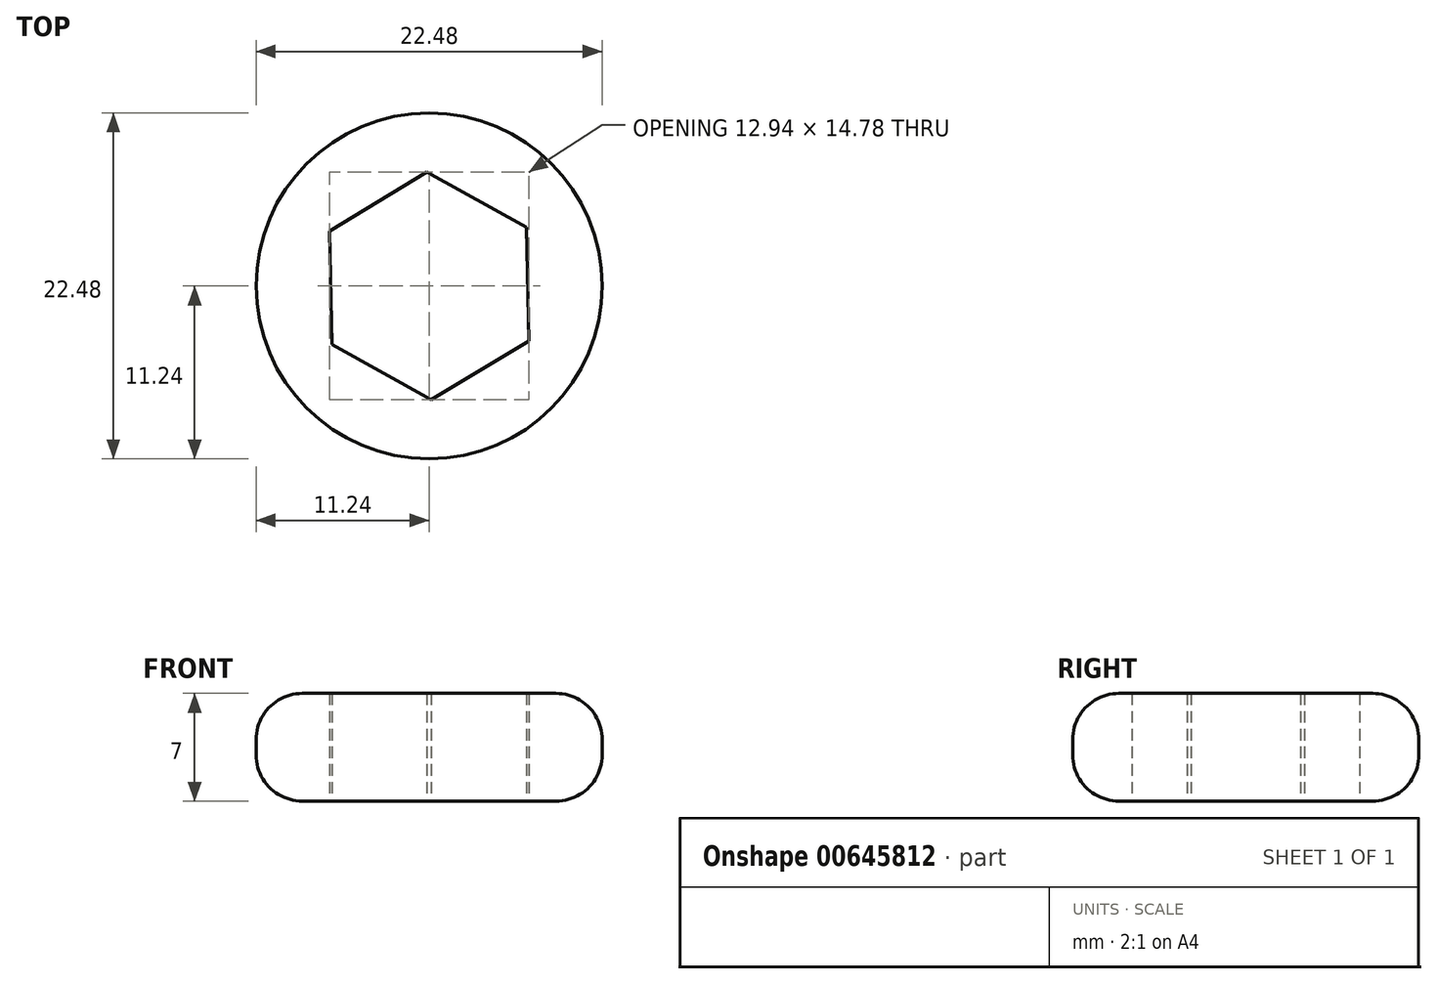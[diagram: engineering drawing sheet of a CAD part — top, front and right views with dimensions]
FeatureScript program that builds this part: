
annotation { "Feature Type Name" : "Feature", "Feature Type Description" : "" }
export const myFeature = defineFeature(function(context is Context, id is Id, definition is map)
    precondition{}
    {
        {
            var Q0;
            Q0=qCreatedBy(makeId("Top.planeOp"),FACE);
            var sketch = newSketch(context, id + "F0", { "sketchPlane" : qUnion([Q0])});
            skCircle(sketch, "E0.cCircle", {"center": v(25, 0) * mm, "radius": 6.4 * mm, "construction": true});
            skLineSegment(sketch, "E0.0", {"start": v(31.47, -3.57) * mm, "end": v(25.14, -7.39) * mm});
            skLineSegment(sketch, "E0.1", {"start": v(25.14, -7.39) * mm, "end": v(18.67, -3.82) * mm});
            skLineSegment(sketch, "E0.2", {"start": v(18.67, -3.82) * mm, "end": v(18.53, 3.57) * mm});
            skLineSegment(sketch, "E0.3", {"start": v(18.53, 3.57) * mm, "end": v(24.86, 7.39) * mm});
            skLineSegment(sketch, "E0.4", {"start": v(24.86, 7.39) * mm, "end": v(31.33, 3.82) * mm});
            skLineSegment(sketch, "E0.5", {"start": v(31.33, 3.82) * mm, "end": v(31.47, -3.57) * mm});
            skPoint(sketch, "E0.0.midPoint", {"position": v(28.3, -5.48) * mm});
            skCircle(sketch, "E1", {"center": v(25, 0) * mm, "radius": 11.24 * mm});
            skArc(sketch, "E2", {"start": v(19.83, -9.98) * mm, "mid": v(16.98, -9.1) * mm, "end": v(14.27, -10.34) * mm});
            skArc(sketch, "E3.MirrorCS", {"start": v(19.83, 9.98) * mm, "mid": v(16.98, 9.1) * mm, "end": v(14.27, 10.34) * mm});
            skCircle(sketch, "E4", {"center": v(0, 0) * mm, "radius": 0.5 * mm});
            skSolve(sketch);
        }
        {
            var Q0;
            {var subQ0=sQuery(id+"F0.wireOp",EDGE,"8972d055-53f9-408d-872e-5fed29d23d3c.2.6");var subQ1=sQuery(id+"F0.wireOp",EDGE,"8972d055-53f9-408d-872e-5fed29d23d3c.1.7");var subQ2=makeQuery(id+"F0.imprint","INTERSECT",VERTEX,{"derivedFrom":[subQ1,subQ0]});Q0=makeQuery(id+"F0.imprint","IMPRINT",FACE,{"disambiguationData":[TD([[makeQuery(id+"F0.imprint","IMPRINT",EDGE,{"disambiguationData":[TD([[subQ2,1.0]])],"derivedFrom":subQ1}),-1.0]])]});}
            var Q1;
            {var subQ0=sQuery(id+"F0.wireOp",EDGE,"8972d055-53f9-408d-872e-5fed29d23d3c.1.12");var subQ1=sQuery(id+"F0.wireOp",EDGE,"8972d055-53f9-408d-872e-5fed29d23d3c.1.10");var subQ2=makeQuery(id+"F0.imprint","INTERSECT",VERTEX,{"disambiguationData":[OD(1.0)],"derivedFrom":[subQ1,subQ0]});Q1=makeQuery(id+"F0.imprint","IMPRINT",FACE,{"disambiguationData":[TD([[makeQuery(id+"F0.imprint","IMPRINT",EDGE,{"disambiguationData":[TD([[subQ2,-1.0]])],"derivedFrom":subQ1}),-1.0]])]});}
            var Q2;
            {var subQ0=sQuery(id+"F0.wireOp",EDGE,"8972d055-53f9-408d-872e-5fed29d23d3c.2.12");var subQ1=sQuery(id+"F0.wireOp",EDGE,"8972d055-53f9-408d-872e-5fed29d23d3c.2.6");var subQ2=makeQuery(id+"F0.imprint","INTERSECT",VERTEX,{"derivedFrom":[subQ1,subQ0]});Q2=makeQuery(id+"F0.imprint","IMPRINT",FACE,{"disambiguationData":[TD([[makeQuery(id+"F0.imprint","IMPRINT",EDGE,{"disambiguationData":[TD([[subQ2,1.0]])],"derivedFrom":subQ1}),-1.0]])]});}
            var Q3;
            Q3=makeQuery(id+"F0.imprint","IMPRINT",FACE,{"disambiguationData":[TD([[makeQuery(id+"F0.imprint","IMPRINT",EDGE,{"derivedFrom":sQuery(id+"F0.wireOp",EDGE,"8972d055-53f9-408d-872e-5fed29d23d3c.1.0")}),1.0]])]});
            var Q4;
            {var subQ0=sQuery(id+"F0.wireOp",EDGE,"8972d055-53f9-408d-872e-5fed29d23d3c.2.6");var subQ1=sQuery(id+"F0.wireOp",EDGE,"8972d055-53f9-408d-872e-5fed29d23d3c.1.10");var subQ2=makeQuery(id+"F0.imprint","INTERSECT",VERTEX,{"disambiguationData":[OD(0.0)],"derivedFrom":[subQ1,subQ0]});Q4=makeQuery(id+"F0.imprint","IMPRINT",FACE,{"disambiguationData":[TD([[makeQuery(id+"F0.imprint","IMPRINT",EDGE,{"disambiguationData":[TD([[subQ2,-1.0]])],"derivedFrom":subQ1}),1.0]])]});}
            var Q5;
            Q5=makeQuery(id+"F0.imprint","IMPRINT",FACE,{"disambiguationData":[TD([[makeQuery(id+"F0.imprint","IMPRINT",EDGE,{"derivedFrom":sQuery(id+"F0.wireOp",EDGE,"8972d055-53f9-408d-872e-5fed29d23d3c.2.4")}),-1.0]])]});
            var Q6;
            Q6=makeQuery(id+"F0.imprint","IMPRINT",FACE,{"disambiguationData":[TD([[makeQuery(id+"F0.imprint","IMPRINT",EDGE,{"derivedFrom":sQuery(id+"F0.wireOp",EDGE,"E0.0")}),1.0]])]});
            var Q7;
            {var subQ0=sQuery(id+"F0.wireOp",EDGE,"E3.MirrorCS");var subQ1=sQuery(id+"F0.wireOp",EDGE,"E1");var subQ2=makeQuery(id+"F0.imprint","INTERSECT",VERTEX,{"disambiguationData":[OD(1.0)],"derivedFrom":[subQ1,subQ0]});Q7=makeQuery(id+"F0.imprint","IMPRINT",FACE,{"disambiguationData":[TD([[makeQuery(id+"F0.imprint","IMPRINT",EDGE,{"disambiguationData":[TD([[subQ2,-1.0]])],"derivedFrom":subQ1}),-1.0]])]});}
            var Q8;
            {var subQ0=sQuery(id+"F0.wireOp",EDGE,"8972d055-53f9-408d-872e-5fed29d23d3c.2.6");var subQ1=sQuery(id+"F0.wireOp",EDGE,"E1");var subQ2=makeQuery(id+"F0.imprint","INTERSECT",VERTEX,{"disambiguationData":[OD(0.0)],"derivedFrom":[subQ1,subQ0]});Q8=makeQuery(id+"F0.imprint","IMPRINT",FACE,{"disambiguationData":[TD([[makeQuery(id+"F0.imprint","IMPRINT",EDGE,{"disambiguationData":[TD([[subQ2,-1.0]])],"derivedFrom":subQ1}),1.0]])]});}
            var Q9;
            {var subQ0=sQuery(id+"F0.wireOp",EDGE,"E2");var subQ1=sQuery(id+"F0.wireOp",EDGE,"E1");var subQ2=makeQuery(id+"F0.imprint","INTERSECT",VERTEX,{"disambiguationData":[OD(1.0)],"derivedFrom":[subQ1,subQ0]});Q9=makeQuery(id+"F0.imprint","IMPRINT",FACE,{"disambiguationData":[TD([[makeQuery(id+"F0.imprint","IMPRINT",EDGE,{"disambiguationData":[TD([[subQ2,1.0]])],"derivedFrom":subQ1}),-1.0]])]});}
            var Q10;
            Q10=makeQuery(id+"F0.imprint","IMPRINT",FACE,{"disambiguationData":[TD([[makeQuery(id+"F0.imprint","IMPRINT",EDGE,{"derivedFrom":sQuery(id+"F0.wireOp",EDGE,"8972d055-53f9-408d-872e-5fed29d23d3c.2.0")}),1.0]])]});
            var Q11;
            {var subQ0=sQuery(id+"F0.wireOp",EDGE,"8972d055-53f9-408d-872e-5fed29d23d3c.2.7");var subQ1=sQuery(id+"F0.wireOp",EDGE,"8972d055-53f9-408d-872e-5fed29d23d3c.2.6");var subQ2=makeQuery(id+"F0.imprint","INTERSECT",VERTEX,{"derivedFrom":[subQ1,subQ0]});Q11=makeQuery(id+"F0.imprint","IMPRINT",FACE,{"disambiguationData":[TD([[makeQuery(id+"F0.imprint","IMPRINT",EDGE,{"disambiguationData":[TD([[subQ2,-1.0]])],"derivedFrom":subQ1}),-1.0]])]});}
            var Q12;
            {var subQ0=sQuery(id+"F0.wireOp",EDGE,"8972d055-53f9-408d-872e-5fed29d23d3c.2.10");var subQ1=sQuery(id+"F0.wireOp",EDGE,"8972d055-53f9-408d-872e-5fed29d23d3c.2.6");var subQ2=makeQuery(id+"F0.imprint","INTERSECT",VERTEX,{"disambiguationData":[OD(0.0)],"derivedFrom":[subQ1,subQ0]});Q12=makeQuery(id+"F0.imprint","IMPRINT",FACE,{"disambiguationData":[TD([[makeQuery(id+"F0.imprint","IMPRINT",EDGE,{"disambiguationData":[TD([[subQ2,1.0]])],"derivedFrom":subQ1}),1.0]])]});}
            var Q13;
            {var subQ0=sQuery(id+"F0.wireOp",EDGE,"E3.MirrorCS");var subQ1=sQuery(id+"F0.wireOp",EDGE,"E1");var subQ2=makeQuery(id+"F0.imprint","INTERSECT",VERTEX,{"disambiguationData":[OD(0.0)],"derivedFrom":[subQ1,subQ0]});Q13=makeQuery(id+"F0.imprint","IMPRINT",FACE,{"disambiguationData":[TD([[makeQuery(id+"F0.imprint","IMPRINT",EDGE,{"disambiguationData":[TD([[subQ2,-1.0]])],"derivedFrom":subQ1}),1.0]])]});}
            var Q14;
            {var subQ0=sQuery(id+"F0.wireOp",EDGE,"E2");var subQ1=sQuery(id+"F0.wireOp",EDGE,"E1");var subQ2=makeQuery(id+"F0.imprint","INTERSECT",VERTEX,{"disambiguationData":[OD(0.0)],"derivedFrom":[subQ1,subQ0]});Q14=makeQuery(id+"F0.imprint","IMPRINT",FACE,{"disambiguationData":[TD([[makeQuery(id+"F0.imprint","IMPRINT",EDGE,{"disambiguationData":[TD([[subQ2,1.0]])],"derivedFrom":subQ1}),1.0]])]});}
            var Q15;
            {var subQ0=sQuery(id+"F0.wireOp",EDGE,"8972d055-53f9-408d-872e-5fed29d23d3c.1.10");var subQ1=sQuery(id+"F0.wireOp",EDGE,"8972d055-53f9-408d-872e-5fed29d23d3c.1.7");var subQ2=makeQuery(id+"F0.imprint","INTERSECT",VERTEX,{"disambiguationData":[OD(0.0)],"derivedFrom":[subQ1,subQ0]});Q15=makeQuery(id+"F0.imprint","IMPRINT",FACE,{"disambiguationData":[TD([[makeQuery(id+"F0.imprint","IMPRINT",EDGE,{"disambiguationData":[TD([[subQ2,-1.0]])],"derivedFrom":subQ1}),1.0]])]});}
            var Q16;
            {var subQ0=sQuery(id+"F0.wireOp",EDGE,"8972d055-53f9-408d-872e-5fed29d23d3c.1.12");var subQ1=sQuery(id+"F0.wireOp",EDGE,"8972d055-53f9-408d-872e-5fed29d23d3c.1.10");var subQ2=makeQuery(id+"F0.imprint","INTERSECT",VERTEX,{"disambiguationData":[OD(0.0)],"derivedFrom":[subQ1,subQ0]});Q16=makeQuery(id+"F0.imprint","IMPRINT",FACE,{"disambiguationData":[TD([[makeQuery(id+"F0.imprint","IMPRINT",EDGE,{"disambiguationData":[TD([[subQ2,-1.0]])],"derivedFrom":subQ1}),1.0]])]});}
            var Q17;
            {var subQ0=sQuery(id+"F0.wireOp",EDGE,"8972d055-53f9-408d-872e-5fed29d23d3c.2.10");var subQ1=sQuery(id+"F0.wireOp",EDGE,"8972d055-53f9-408d-872e-5fed29d23d3c.2.7");var subQ2=makeQuery(id+"F0.imprint","INTERSECT",VERTEX,{"disambiguationData":[OD(0.0)],"derivedFrom":[subQ1,subQ0]});Q17=makeQuery(id+"F0.imprint","IMPRINT",FACE,{"disambiguationData":[TD([[makeQuery(id+"F0.imprint","IMPRINT",EDGE,{"disambiguationData":[TD([[subQ2,-1.0]])],"derivedFrom":subQ1}),1.0]])]});}
            var Q18;
            {var subQ0=sQuery(id+"F0.wireOp",EDGE,"8972d055-53f9-408d-872e-5fed29d23d3c.2.12");var subQ1=sQuery(id+"F0.wireOp",EDGE,"8972d055-53f9-408d-872e-5fed29d23d3c.2.10");var subQ2=makeQuery(id+"F0.imprint","INTERSECT",VERTEX,{"disambiguationData":[OD(0.0)],"derivedFrom":[subQ1,subQ0]});Q18=makeQuery(id+"F0.imprint","IMPRINT",FACE,{"disambiguationData":[TD([[makeQuery(id+"F0.imprint","IMPRINT",EDGE,{"disambiguationData":[TD([[subQ2,-1.0]])],"derivedFrom":subQ1}),1.0]])]});}
            extrude(context, id + "F1", {"entities" : qUnion([Q0, Q1, Q2, Q3, Q4, Q5, Q6, Q7, Q8, Q9, Q10, Q11, Q12, Q13, Q14, Q15, Q16, Q17, Q18]), "depth" : 7 * mm, "offsetDistance" : 25 * mm});
        }
        {
            var Q0;
            Q0=makeQuery(id+"F1.opExtrude","CAP_EDGE",EDGE,{"disambiguationData":[OSD([sQuery(id+"F0.wireOp",EDGE,"8972d055-53f9-408d-872e-5fed29d23d3c.2.10")])],"isStart":false});
            var Q1;
            {var subQ0=sQuery(id+"F0.wireOp",EDGE,"8972d055-53f9-408d-872e-5fed29d23d3c.2.6");Q1=makeQuery(id+"F1.opExtrude","CAP_EDGE",EDGE,{"disambiguationData":[OSD([subQ0]),TDD([makeQuery(id+"F0.imprint","IMPRINT",EDGE,{"disambiguationData":[TD([[makeQuery(id+"F0.imprint","INTERSECT",VERTEX,{"derivedFrom":[sQuery(id+"F0.wireOp",EDGE,"E2"),subQ0]}),1.0]])],"derivedFrom":subQ0})])],"isStart":false});}
            var Q2;
            Q2=makeQuery(id+"F1.opExtrude","CAP_EDGE",EDGE,{"disambiguationData":[OSD([sQuery(id+"F0.wireOp",EDGE,"8972d055-53f9-408d-872e-5fed29d23d3c.2.12")])],"isStart":false});
            var Q3;
            Q3=makeQuery(id+"F1.opExtrude","CAP_EDGE",EDGE,{"disambiguationData":[OSD([sQuery(id+"F0.wireOp",EDGE,"E2")])],"isStart":false});
            var Q4;
            Q4=makeQuery(id+"F1.opExtrude","CAP_EDGE",EDGE,{"disambiguationData":[OSD([sQuery(id+"F0.wireOp",EDGE,"E2")])],"isStart":true});
            var Q5;
            {var subQ0=sQuery(id+"F0.wireOp",EDGE,"8972d055-53f9-408d-872e-5fed29d23d3c.2.6");Q5=makeQuery(id+"F1.opExtrude","CAP_EDGE",EDGE,{"disambiguationData":[OSD([subQ0]),TDD([makeQuery(id+"F0.imprint","IMPRINT",EDGE,{"disambiguationData":[TD([[makeQuery(id+"F0.imprint","INTERSECT",VERTEX,{"derivedFrom":[sQuery(id+"F0.wireOp",EDGE,"E2"),subQ0]}),1.0]])],"derivedFrom":subQ0})])],"isStart":true});}
            var Q6;
            Q6=makeQuery(id+"F1.opExtrude","CAP_EDGE",EDGE,{"disambiguationData":[OSD([sQuery(id+"F0.wireOp",EDGE,"8972d055-53f9-408d-872e-5fed29d23d3c.2.12")])],"isStart":true});
            var Q7;
            Q7=makeQuery(id+"F1.opExtrude","CAP_EDGE",EDGE,{"disambiguationData":[OSD([sQuery(id+"F0.wireOp",EDGE,"8972d055-53f9-408d-872e-5fed29d23d3c.2.10")])],"isStart":true});
            var Q8;
            Q8=makeQuery(id+"F1.opExtrude","CAP_EDGE",EDGE,{"disambiguationData":[OSD([sQuery(id+"F0.wireOp",EDGE,"8972d055-53f9-408d-872e-5fed29d23d3c.2.7")])],"isStart":false});
            var Q9;
            {var subQ0=sQuery(id+"F0.wireOp",EDGE,"8972d055-53f9-408d-872e-5fed29d23d3c.2.6");Q9=makeQuery(id+"F1.opExtrude","CAP_EDGE",EDGE,{"disambiguationData":[OSD([subQ0]),TDD([makeQuery(id+"F0.imprint","IMPRINT",EDGE,{"disambiguationData":[TD([[makeQuery(id+"F0.imprint","INTERSECT",VERTEX,{"derivedFrom":[sQuery(id+"F0.wireOp",EDGE,"8972d055-53f9-408d-872e-5fed29d23d3c.1.12"),subQ0]}),-1.0]])],"derivedFrom":subQ0})])],"isStart":false});}
            var Q10;
            Q10=makeQuery(id+"F1.opExtrude","CAP_EDGE",EDGE,{"disambiguationData":[OSD([sQuery(id+"F0.wireOp",EDGE,"8972d055-53f9-408d-872e-5fed29d23d3c.1.12")])],"isStart":false});
            var Q11;
            Q11=makeQuery(id+"F1.opExtrude","CAP_EDGE",EDGE,{"disambiguationData":[OSD([sQuery(id+"F0.wireOp",EDGE,"8972d055-53f9-408d-872e-5fed29d23d3c.1.10")])],"isStart":false});
            var Q12;
            Q12=makeQuery(id+"F1.opExtrude","CAP_EDGE",EDGE,{"disambiguationData":[OSD([sQuery(id+"F0.wireOp",EDGE,"8972d055-53f9-408d-872e-5fed29d23d3c.1.7")])],"isStart":false});
            var Q13;
            {var subQ0=sQuery(id+"F0.wireOp",EDGE,"8972d055-53f9-408d-872e-5fed29d23d3c.2.6");Q13=makeQuery(id+"F1.opExtrude","CAP_EDGE",EDGE,{"disambiguationData":[OSD([subQ0]),TDD([makeQuery(id+"F0.imprint","IMPRINT",EDGE,{"disambiguationData":[TD([[makeQuery(id+"F0.imprint","INTERSECT",VERTEX,{"derivedFrom":[sQuery(id+"F0.wireOp",EDGE,"E3.MirrorCS"),subQ0]}),-1.0]])],"derivedFrom":subQ0})])],"isStart":false});}
            var Q14;
            Q14=makeQuery(id+"F1.opExtrude","CAP_EDGE",EDGE,{"disambiguationData":[OSD([sQuery(id+"F0.wireOp",EDGE,"E3.MirrorCS")])],"isStart":false});
            var Q15;
            Q15=makeQuery(id+"F1.opExtrude","CAP_EDGE",EDGE,{"disambiguationData":[OSD([sQuery(id+"F0.wireOp",EDGE,"E1")])],"isStart":false});
            var Q16;
            Q16=makeQuery(id+"F1.opExtrude","CAP_EDGE",EDGE,{"disambiguationData":[OSD([sQuery(id+"F0.wireOp",EDGE,"E1")])],"isStart":true});
            var Q17;
            Q17=makeQuery(id+"F1.opExtrude","CAP_EDGE",EDGE,{"disambiguationData":[OSD([sQuery(id+"F0.wireOp",EDGE,"8972d055-53f9-408d-872e-5fed29d23d3c.2.7")])],"isStart":true});
            var Q18;
            {var subQ0=sQuery(id+"F0.wireOp",EDGE,"8972d055-53f9-408d-872e-5fed29d23d3c.2.6");Q18=makeQuery(id+"F1.opExtrude","CAP_EDGE",EDGE,{"disambiguationData":[OSD([subQ0]),TDD([makeQuery(id+"F0.imprint","IMPRINT",EDGE,{"disambiguationData":[TD([[makeQuery(id+"F0.imprint","INTERSECT",VERTEX,{"derivedFrom":[sQuery(id+"F0.wireOp",EDGE,"8972d055-53f9-408d-872e-5fed29d23d3c.1.12"),subQ0]}),-1.0]])],"derivedFrom":subQ0})])],"isStart":true});}
            var Q19;
            Q19=makeQuery(id+"F1.opExtrude","CAP_EDGE",EDGE,{"disambiguationData":[OSD([sQuery(id+"F0.wireOp",EDGE,"8972d055-53f9-408d-872e-5fed29d23d3c.1.12")])],"isStart":true});
            var Q20;
            Q20=makeQuery(id+"F1.opExtrude","CAP_EDGE",EDGE,{"disambiguationData":[OSD([sQuery(id+"F0.wireOp",EDGE,"8972d055-53f9-408d-872e-5fed29d23d3c.1.10")])],"isStart":true});
            var Q21;
            Q21=makeQuery(id+"F1.opExtrude","CAP_EDGE",EDGE,{"disambiguationData":[OSD([sQuery(id+"F0.wireOp",EDGE,"E3.MirrorCS")])],"isStart":true});
            var Q22;
            Q22=makeQuery(id+"F1.opExtrude","CAP_EDGE",EDGE,{"disambiguationData":[OSD([sQuery(id+"F0.wireOp",EDGE,"8972d055-53f9-408d-872e-5fed29d23d3c.1.7")])],"isStart":true});
            var Q23;
            {var subQ0=sQuery(id+"F0.wireOp",EDGE,"8972d055-53f9-408d-872e-5fed29d23d3c.2.6");Q23=makeQuery(id+"F1.opExtrude","CAP_EDGE",EDGE,{"disambiguationData":[OSD([subQ0]),TDD([makeQuery(id+"F0.imprint","IMPRINT",EDGE,{"disambiguationData":[TD([[makeQuery(id+"F0.imprint","INTERSECT",VERTEX,{"derivedFrom":[sQuery(id+"F0.wireOp",EDGE,"E3.MirrorCS"),subQ0]}),-1.0]])],"derivedFrom":subQ0})])],"isStart":true});}
            fillet(context, id + "F2", {"entities" : qUnion([Q0, Q1, Q2, Q3, Q4, Q5, Q6, Q7, Q8, Q9, Q10, Q11, Q12, Q13, Q14, Q15, Q16, Q17, Q18, Q19, Q20, Q21, Q22, Q23]), "radius" : 3 * mm, "tangentPropagation" : true, "allowEdgeOverflow" : false});
        }
    });
